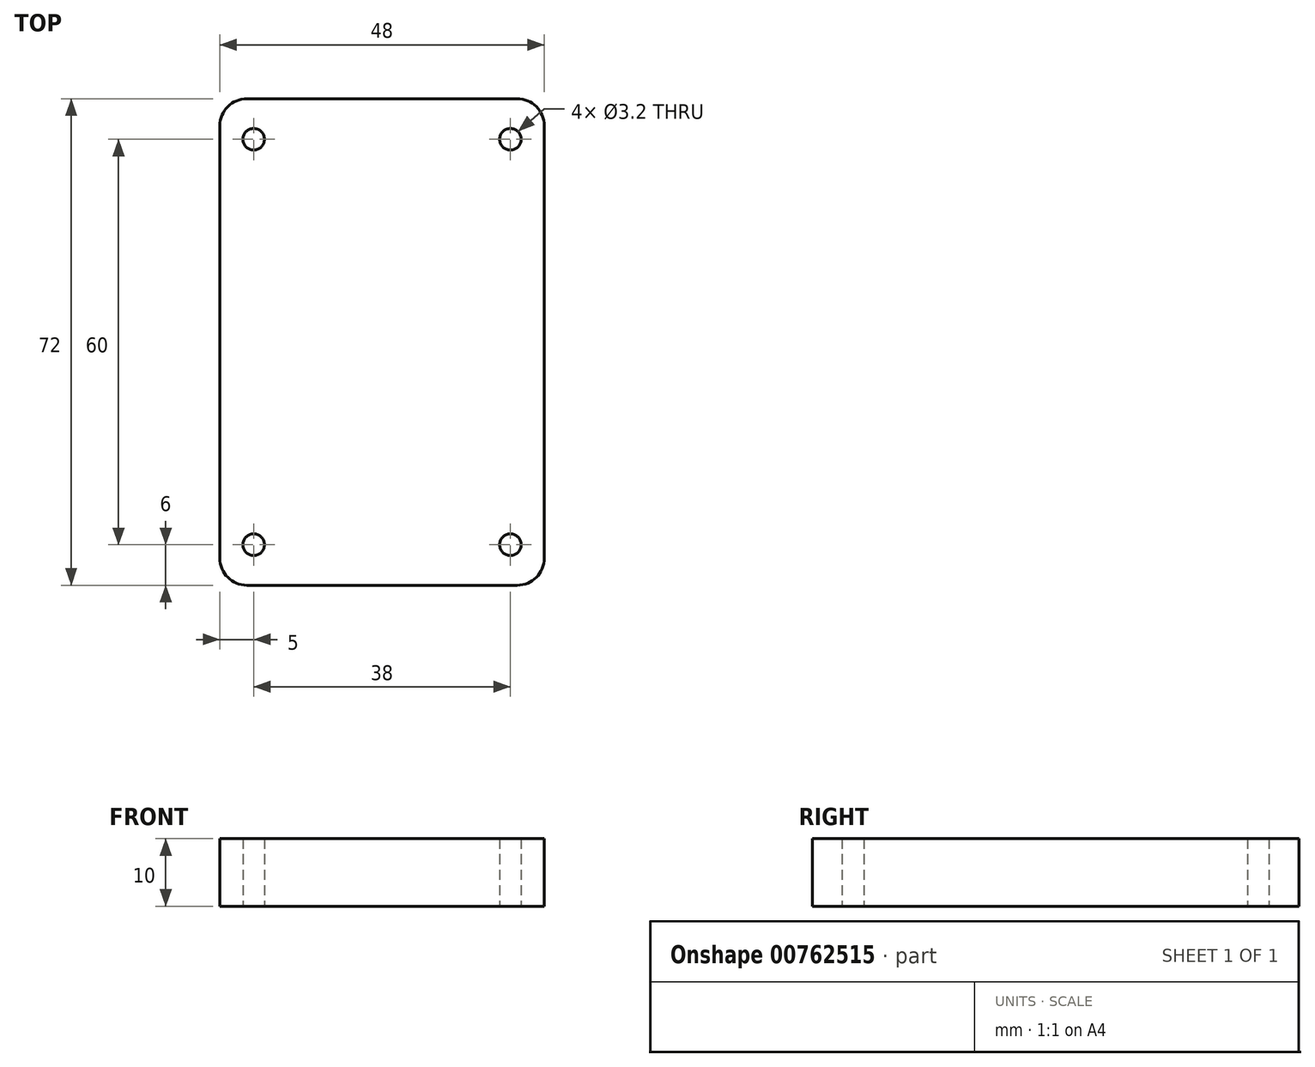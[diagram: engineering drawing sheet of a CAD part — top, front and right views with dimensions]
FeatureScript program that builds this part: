
annotation { "Feature Type Name" : "Feature", "Feature Type Description" : "" }
export const myFeature = defineFeature(function(context is Context, id is Id, definition is map)
    precondition{}
    {
        {
            var Q0;
            Q0=qCreatedBy(makeId("Top.planeOp"),FACE);
            var sketch = newSketch(context, id + "F0", { "sketchPlane" : qUnion([Q0])});
            skCircle(sketch, "E0", {"center": v(19, 30) * mm, "radius": 1.6 * mm});
            skLineSegment(sketch, "E1", {"start": v(0, 36) * mm, "end": v(20, 36) * mm});
            skLineSegment(sketch, "E2", {"start": v(24, 32) * mm, "end": v(24, 0) * mm});
            skArc(sketch, "E3.filletArc", {"start": v(24, 32) * mm, "mid": v(22.83, 34.83) * mm, "end": v(20, 36) * mm});
            skLineSegment(sketch, "E4.MirrorCS", {"start": v(0, 36) * mm, "end": v(-20, 36) * mm});
            skArc(sketch, "E5.MirrorCS", {"start": v(-24, 32) * mm, "mid": v(-22.83, 34.83) * mm, "end": v(-20, 36) * mm});
            skLineSegment(sketch, "E6.MirrorCS", {"start": v(-24, 32) * mm, "end": v(-24, 0) * mm});
            skCircle(sketch, "E7.MirrorC", {"center": v(-19, 30) * mm, "radius": 1.6 * mm});
            skLineSegment(sketch, "E8.MirrorCS", {"start": v(-24, -32) * mm, "end": v(-24, 0) * mm});
            skArc(sketch, "E9.MirrorCS", {"start": v(-24, -32) * mm, "mid": v(-22.83, -34.83) * mm, "end": v(-20, -36) * mm});
            skLineSegment(sketch, "E10.MirrorCS", {"start": v(0, -36) * mm, "end": v(-20, -36) * mm});
            skLineSegment(sketch, "E11.MirrorCS", {"start": v(0, -36) * mm, "end": v(20, -36) * mm});
            skArc(sketch, "E12.MirrorCS", {"start": v(24, -32) * mm, "mid": v(22.83, -34.83) * mm, "end": v(20, -36) * mm});
            skLineSegment(sketch, "E13.MirrorCS", {"start": v(24, -32) * mm, "end": v(24, 0) * mm});
            skCircle(sketch, "E14.MirrorC", {"center": v(19, -30) * mm, "radius": 1.6 * mm});
            skCircle(sketch, "E15.MirrorC", {"center": v(-19, -30) * mm, "radius": 1.6 * mm});
            skSolve(sketch);
        }
        {
            var Q0;
            Q0 = qSketchRegion(id + "F0", true);
            extrude(context, id + "F1", {"entities" : qUnion([Q0]), "depth" : 10 * mm, "offsetDistance" : 25 * mm});
        }
    });
